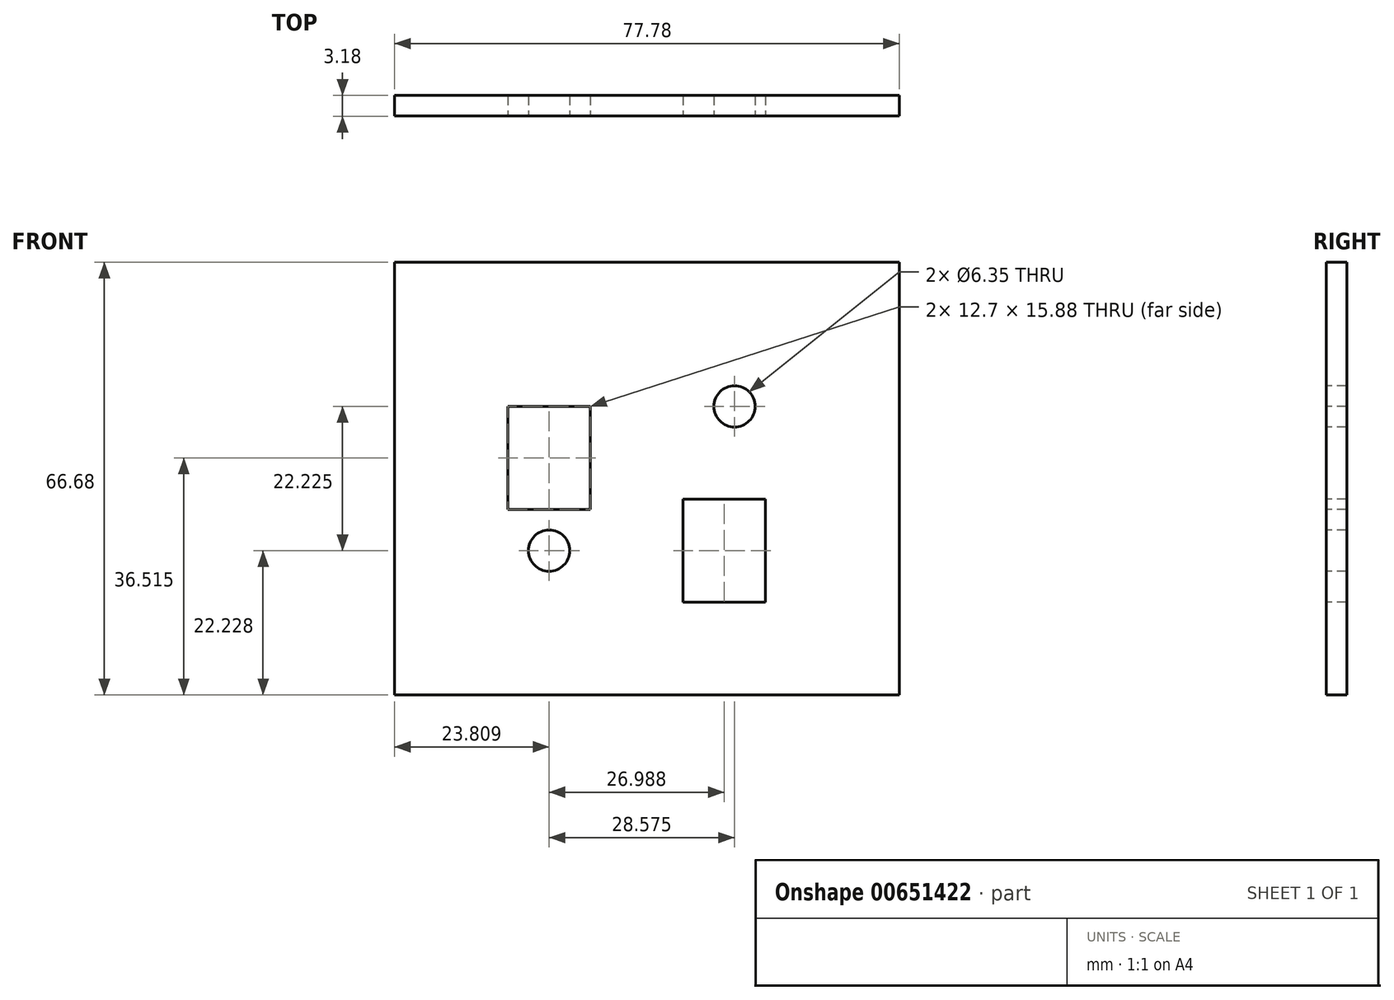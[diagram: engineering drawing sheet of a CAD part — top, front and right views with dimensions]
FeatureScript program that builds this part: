
annotation { "Feature Type Name" : "Feature", "Feature Type Description" : "" }
export const myFeature = defineFeature(function(context is Context, id is Id, definition is map)
    precondition{}
    {
        {
            var Q0;
            Q0=qCreatedBy(makeId("Front.planeOp"),FACE);
            var sketch = newSketch(context, id + "F0", { "sketchPlane" : qUnion([Q0])});
            skLineSegment(sketch, "E0.bottom", {"start": v(38.9, 33.34) * mm, "end": v(-38.9, 33.34) * mm});
            skLineSegment(sketch, "E0.top", {"start": v(38.9, -33.34) * mm, "end": v(-38.9, -33.34) * mm});
            skLineSegment(sketch, "E0.left", {"start": v(38.9, 33.34) * mm, "end": v(38.9, -33.34) * mm});
            skLineSegment(sketch, "E0.right", {"start": v(-38.9, 33.34) * mm, "end": v(-38.9, -33.34) * mm});
            skPoint(sketch, "E0.middle", {"position": v(0, 0) * mm});
            skSolve(sketch);
        }
        {
            var Q0;
            Q0=qSketchRegion(id+"F0",true);
            extrude(context, id + "F1", {"entities" : qUnion([Q0]), "depth" : 3.17 * mm, "offsetDistance" : 25.4 * mm});
        }
        {
            var Q0;
            Q0=makeQuery(id+"F1.opExtrude","CAP_FACE",FACE,{"disambiguationData":[OSD([sQuery(id+"F0.wireOp",EDGE,"E0.bottom"),sQuery(id+"F0.wireOp",EDGE,"E0.top"),sQuery(id+"F0.wireOp",EDGE,"E0.left"),sQuery(id+"F0.wireOp",EDGE,"E0.right")])],"isStart":false});
            var sketch = newSketch(context, id + "F2", { "sketchPlane" : qUnion([Q0])});
            skPoint(sketch, "E1", {"position": v(-15.08, -11.11) * mm});
            skSolve(sketch);
        }
        {
            var Q0;
            Q0=sQuery(id+"F2.wireOp",VERTEX,"E1");
            var Q1;
            Q1=makeQuery(id+"F1.opExtrude","SWEPT_BODY",BODY,{"disambiguationData":[OSD([sQuery(id+"F0.wireOp",EDGE,"E0.bottom"),sQuery(id+"F0.wireOp",EDGE,"E0.top"),sQuery(id+"F0.wireOp",EDGE,"E0.left"),sQuery(id+"F0.wireOp",EDGE,"E0.right")])]});
            hole(context, id + "F3", {"style" : HoleStyle.SIMPLE, "endStyle" : HoleEndStyle.THROUGH, "holeDiameter" : 6.35 * mm, "majorDiameter" : 6.35 * mm, "isTappedThrough" : true, "tappedDepth" : 12.7 * mm, "tapClearance" : 3, "locations" : qUnion([Q0]), "scope" : qUnion([Q1])});
        }
        {
            var Q0;
            Q0=makeQuery(id+"F1.opExtrude","CAP_FACE",FACE,{"disambiguationData":[OSD([sQuery(id+"F0.wireOp",EDGE,"E0.bottom"),sQuery(id+"F0.wireOp",EDGE,"E0.top"),sQuery(id+"F0.wireOp",EDGE,"E0.left"),sQuery(id+"F0.wireOp",EDGE,"E0.right")])],"isStart":false});
            var sketch = newSketch(context, id + "F4", { "sketchPlane" : qUnion([Q0])});
            skPoint(sketch, "E2", {"position": v(13.5, 11.11) * mm});
            skSolve(sketch);
        }
        {
            var Q0;
            Q0=sQuery(id+"F4.wireOp",VERTEX,"E2");
            var Q1;
            Q1=makeQuery(id+"F1.opExtrude","SWEPT_BODY",BODY,{"disambiguationData":[OSD([sQuery(id+"F0.wireOp",EDGE,"E0.bottom"),sQuery(id+"F0.wireOp",EDGE,"E0.top"),sQuery(id+"F0.wireOp",EDGE,"E0.left"),sQuery(id+"F0.wireOp",EDGE,"E0.right")])]});
            hole(context, id + "F5", {"style" : HoleStyle.SIMPLE, "endStyle" : HoleEndStyle.THROUGH, "holeDiameter" : 6.35 * mm, "majorDiameter" : 6.35 * mm, "isTappedThrough" : true, "tappedDepth" : 12.7 * mm, "tapClearance" : 3, "locations" : qUnion([Q0]), "scope" : qUnion([Q1])});
        }
        {
            var Q0;
            Q0=makeQuery(id+"F1.opExtrude","CAP_FACE",FACE,{"disambiguationData":[OSD([sQuery(id+"F0.wireOp",EDGE,"E0.bottom"),sQuery(id+"F0.wireOp",EDGE,"E0.top"),sQuery(id+"F0.wireOp",EDGE,"E0.left"),sQuery(id+"F0.wireOp",EDGE,"E0.right")])],"isStart":false});
            var sketch = newSketch(context, id + "F6", { "sketchPlane" : qUnion([Q0])});
            skLineSegment(sketch, "E3.bottom", {"start": v(-21.43, 11.11) * mm, "end": v(-8.73, 11.11) * mm});
            skLineSegment(sketch, "E3.top", {"start": v(-21.43, -4.76) * mm, "end": v(-8.73, -4.76) * mm});
            skLineSegment(sketch, "E3.left", {"start": v(-21.43, 11.11) * mm, "end": v(-21.43, -4.76) * mm});
            skLineSegment(sketch, "E3.right", {"start": v(-8.73, 11.11) * mm, "end": v(-8.73, -4.76) * mm});
            skLineSegment(sketch, "E4.bottom", {"start": v(5.56, -3.17) * mm, "end": v(18.26, -3.17) * mm});
            skLineSegment(sketch, "E4.top", {"start": v(5.56, -19.05) * mm, "end": v(18.26, -19.05) * mm});
            skLineSegment(sketch, "E4.left", {"start": v(5.56, -3.17) * mm, "end": v(5.56, -19.05) * mm});
            skLineSegment(sketch, "E4.right", {"start": v(18.26, -3.17) * mm, "end": v(18.26, -19.05) * mm});
            skSolve(sketch);
        }
        {
            var Q0;
            Q0 = qSketchRegion(id + "F6", true);
            extrude(context, id + "F7", {"entities" : qUnion([Q0]), "operationType" : NewBodyOperationType.REMOVE, "endBound" : BoundingType.THROUGH_ALL, "oppositeDirection" : true, "depth" : 25.4 * mm, "offsetDistance" : 25.4 * mm});
        }
    });
